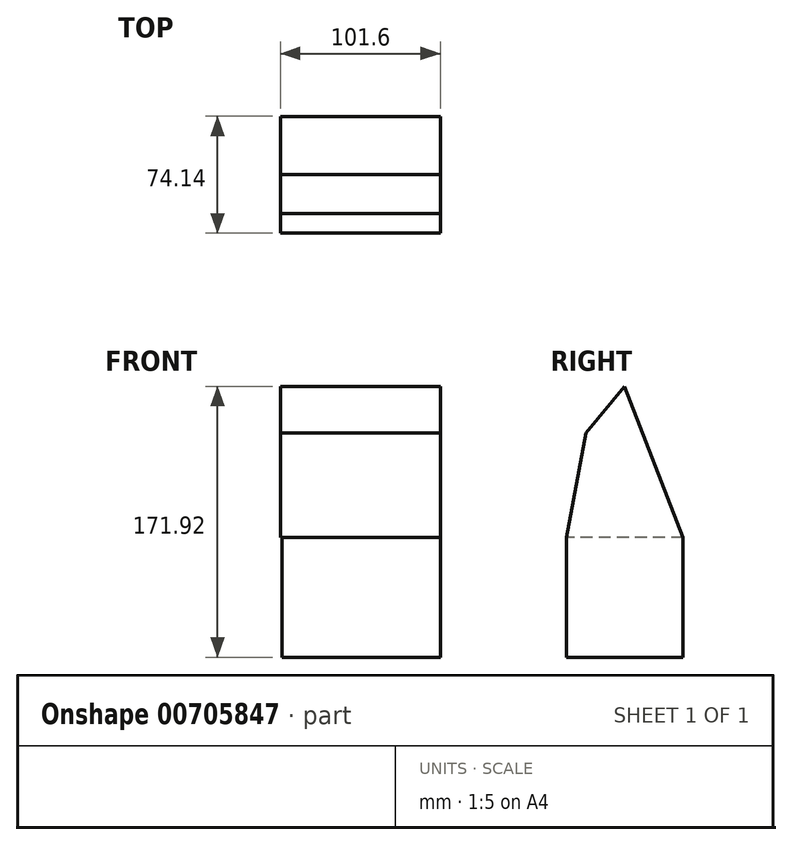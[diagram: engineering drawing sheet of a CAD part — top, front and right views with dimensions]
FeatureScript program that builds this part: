
annotation { "Feature Type Name" : "Feature", "Feature Type Description" : "" }
export const myFeature = defineFeature(function(context is Context, id is Id, definition is map)
    precondition{}
    {
        {
            var Q0;
            Q0=qCreatedBy(makeId("Top.planeOp"),FACE);
            var sketch = newSketch(context, id + "F0", { "sketchPlane" : qUnion([Q0])});
            skLineSegment(sketch, "E0.bottom", {"start": v(50.23, 37.07) * mm, "end": v(-50.23, 37.07) * mm});
            skLineSegment(sketch, "E0.top", {"start": v(50.23, -37.07) * mm, "end": v(-50.23, -37.07) * mm});
            skLineSegment(sketch, "E0.left", {"start": v(50.23, 37.07) * mm, "end": v(50.23, -37.07) * mm});
            skLineSegment(sketch, "E0.right", {"start": v(-50.23, 37.07) * mm, "end": v(-50.23, -37.07) * mm});
            skPoint(sketch, "E0.middle", {"position": v(0, 0) * mm});
            skSolve(sketch);
        }
        {
            var Q0;
            Q0 = qSketchRegion(id + "F0", true);
            extrude(context, id + "F1", {"entities" : qUnion([Q0]), "depth" : 76.2 * mm, "offsetDistance" : 25.4 * mm});
        }
        {
            var Q0;
            Q0=makeQuery(id+"F1.opExtrude","SWEPT_FACE",FACE,{"disambiguationData":[OSD([sQuery(id+"F0.wireOp",EDGE,"E0.left")])]});
            var sketch = newSketch(context, id + "F2", { "sketchPlane" : qUnion([Q0])});
            skLineSegment(sketch, "E1", {"start": v(0, 171.92) * mm, "end": v(37.07, 76.2) * mm});
            skLineSegment(sketch, "E2", {"start": v(37.07, 76.2) * mm, "end": v(-37.07, 76.2) * mm});
            skLineSegment(sketch, "E3", {"start": v(-37.07, 76.2) * mm, "end": v(-24.67, 142.54) * mm});
            skLineSegment(sketch, "E4", {"start": v(-24.67, 142.54) * mm, "end": v(0, 171.92) * mm});
            skSolve(sketch);
        }
        {
            var Q0;
            Q0 = qSketchRegion(id + "F2", true);
            extrude(context, id + "F3", {"entities" : qUnion([Q0]), "operationType" : NewBodyOperationType.ADD, "oppositeDirection" : true, "depth" : 101.6 * mm, "offsetDistance" : 25.4 * mm});
        }
    });
